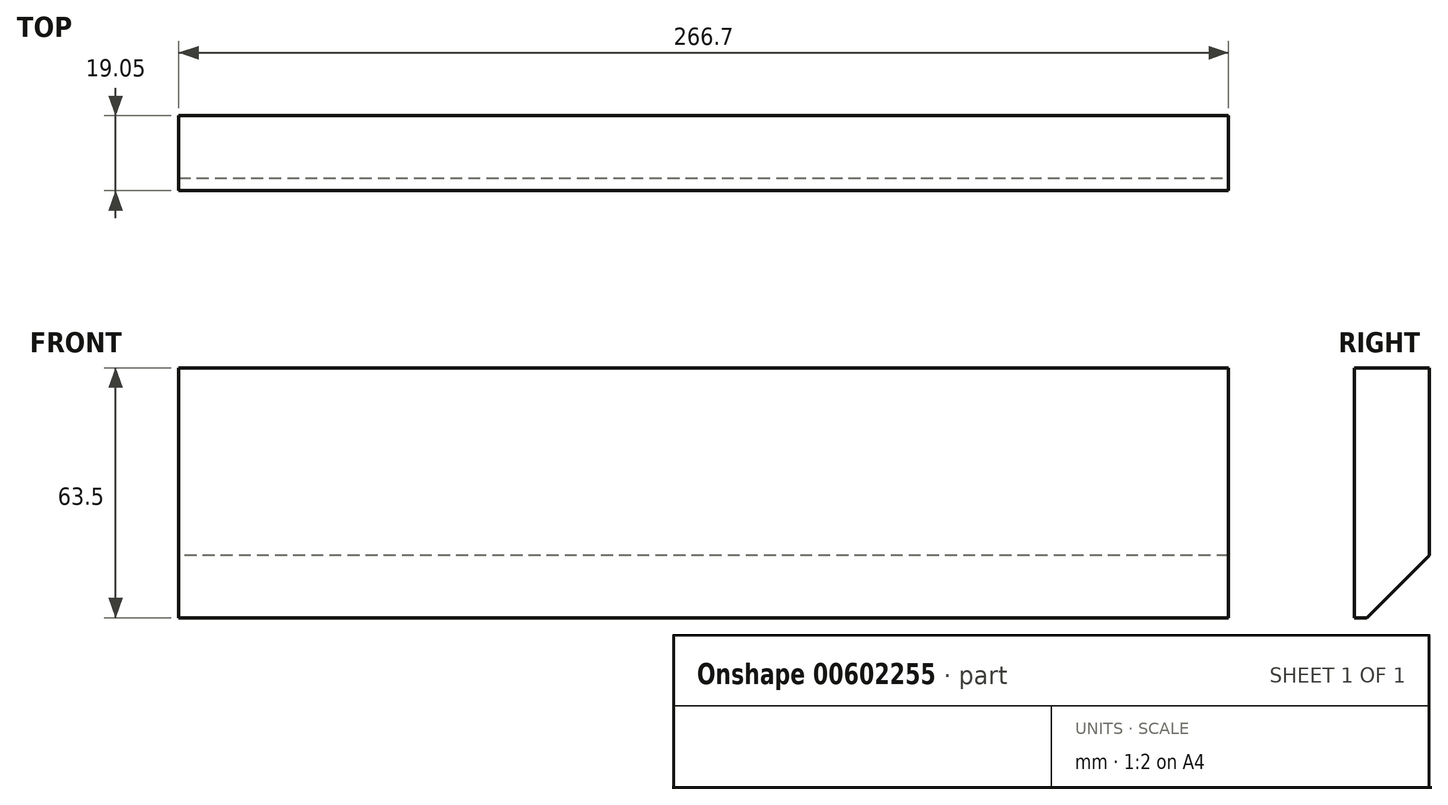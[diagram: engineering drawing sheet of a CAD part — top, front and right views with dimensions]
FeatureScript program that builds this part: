
annotation { "Feature Type Name" : "Feature", "Feature Type Description" : "" }
export const myFeature = defineFeature(function(context is Context, id is Id, definition is map)
    precondition{}
    {
        {
            var Q0;
            Q0=qCreatedBy(makeId("Right.planeOp"),FACE);
            var sketch = newSketch(context, id + "F0", { "sketchPlane" : qUnion([Q0])});
            skLineSegment(sketch, "E0.bottom", {"start": v(0, 0) * mm, "end": v(19.05, 0) * mm});
            skLineSegment(sketch, "E0.top", {"start": v(0, 63.5) * mm, "end": v(19.05, 63.5) * mm});
            skLineSegment(sketch, "E0.left", {"start": v(0, 0) * mm, "end": v(0, 63.5) * mm});
            skLineSegment(sketch, "E0.right", {"start": v(19.05, 0) * mm, "end": v(19.05, 63.5) * mm});
            skSolve(sketch);
        }
        {
            var Q0;
            Q0 = qSketchRegion(id + "F0", true);
            extrude(context, id + "F1", {"entities" : qUnion([Q0]), "oppositeDirection" : true, "depth" : 266.7 * mm, "offsetDistance" : 25.4 * mm});
        }
        {
            var Q0;
            Q0=makeQuery(id+"F1.opExtrude","SWEPT_EDGE",EDGE,{"disambiguationData":[OSD([sQuery(id+"F0.wireOp",EDGE,"E0.bottom"),sQuery(id+"F0.wireOp",EDGE,"E0.right")])]});
            chamfer(context, id + "F2", {"entities" : qUnion([Q0]), "chamferType" : ChamferType.TWO_OFFSETS, "width1" : 15.88 * mm, "oppositeDirection" : false, "width2" : 15.88 * mm, "tangentPropagation" : true});
        }
    });
